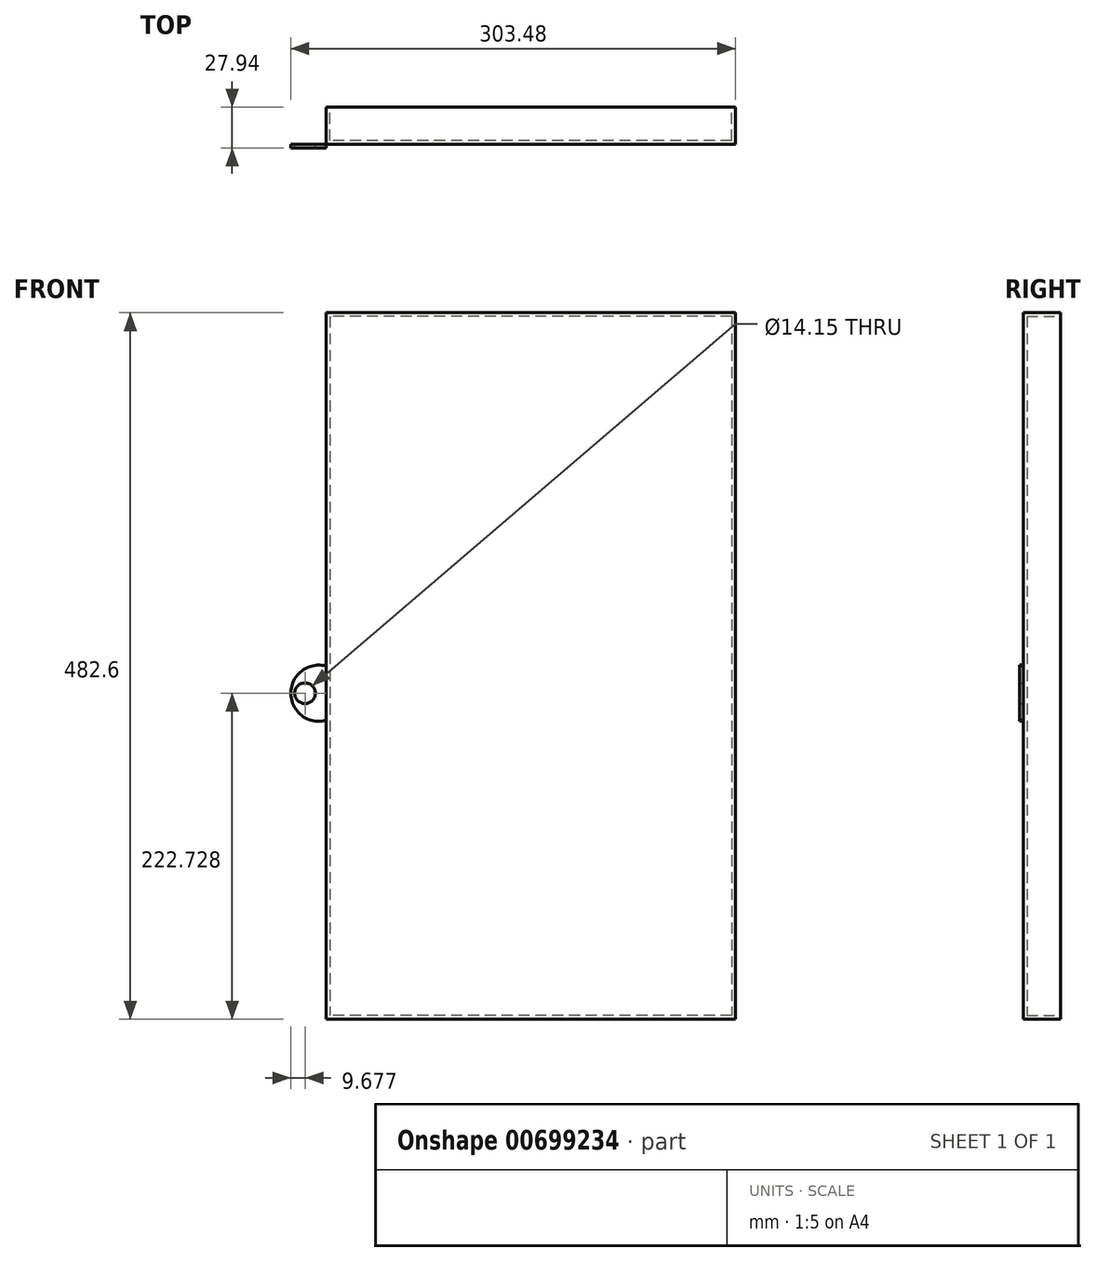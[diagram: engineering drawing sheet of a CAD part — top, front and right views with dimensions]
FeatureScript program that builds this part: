
annotation { "Feature Type Name" : "Feature", "Feature Type Description" : "" }
export const myFeature = defineFeature(function(context is Context, id is Id, definition is map)
    precondition{}
    {
        {
            var Q0;
            Q0=qCreatedBy(makeId("Front.planeOp"),FACE);
            var sketch = newSketch(context, id + "F0", { "sketchPlane" : qUnion([Q0])});
            skLineSegment(sketch, "E0.bottom", {"start": v(150.12, 241.3) * mm, "end": v(-129.28, 241.3) * mm});
            skLineSegment(sketch, "E0.top", {"start": v(150.12, -241.3) * mm, "end": v(-129.28, -241.3) * mm});
            skLineSegment(sketch, "E0.left", {"start": v(150.12, 241.3) * mm, "end": v(150.12, -241.3) * mm});
            skLineSegment(sketch, "E0.right", {"start": v(-129.28, 241.3) * mm, "end": v(-129.28, -241.3) * mm});
            skPoint(sketch, "E0.middle", {"position": v(10.42, 0) * mm});
            skPoint(sketch, "E1.end.orphan", {"position": v(-129.28, 0) * mm});
            skSolve(sketch);
        }
        {
            var Q0;
            {var subQ1=sQuery(id+"F0.wireOp",EDGE,"E0.bottom");Q0=makeQuery(id+"F0.imprint","IMPRINT",FACE,{"disambiguationData":[TD([[makeQuery(id+"F0.imprint","IMPRINT",EDGE,{"derivedFrom":subQ1}),1.0]])]});}
            extrude(context, id + "F1", {"entities" : qUnion([Q0]), "depth" : 25.4 * mm, "offsetDistance" : 25.4 * mm});
        }
        {
            var Q0;
            Q0=makeQuery(id+"F1.opExtrude","CAP_FACE",FACE,{"disambiguationData":[OSD([sQuery(id+"F0.wireOp",EDGE,"E0.bottom"),sQuery(id+"F0.wireOp",EDGE,"E0.top"),sQuery(id+"F0.wireOp",EDGE,"E0.left"),sQuery(id+"F0.wireOp",EDGE,"E0.right"),sQuery(id+"F0.wireOp",EDGE,"E1")])],"isStart":true});
            shell(context, id + "F2", {"entities" : qUnion([Q0]), "thickness" : 2.54 * mm});
        }
        {
            var Q0;
            Q0=makeQuery(id+"F1.opExtrude","CAP_FACE",FACE,{"disambiguationData":[OSD([sQuery(id+"F0.wireOp",EDGE,"E0.bottom"),sQuery(id+"F0.wireOp",EDGE,"E0.top"),sQuery(id+"F0.wireOp",EDGE,"E0.left"),sQuery(id+"F0.wireOp",EDGE,"E0.right")])],"isStart":false});
            var sketch = newSketch(context, id + "F3", { "sketchPlane" : qUnion([Q0])});
            skArc(sketch, "E2", {"start": v(-129.28, 0) * mm, "mid": v(-153.36, -18.57) * mm, "end": v(-129.28, -37.14) * mm});
            skPoint(sketch, "E3", {"position": v(-143.68, -18.57) * mm});
            skCircle(sketch, "E4", {"center": v(-143.68, -18.57) * mm, "radius": 7.07 * mm});
            skSolve(sketch);
        }
        {
            var Q0;
            {var subQ0=sQuery(id+"F3.wireOp",EDGE,"E2");Q0=makeQuery(id+"F3.imprint","IMPRINT",FACE,{"disambiguationData":[TD([[makeQuery(id+"F3.imprint","IMPRINT",EDGE,{"derivedFrom":subQ0}),1.0]])]});}
            extrude(context, id + "F4", {"entities" : qUnion([Q0]), "depth" : 2.54 * mm, "offsetDistance" : 25.4 * mm});
        }
    });
